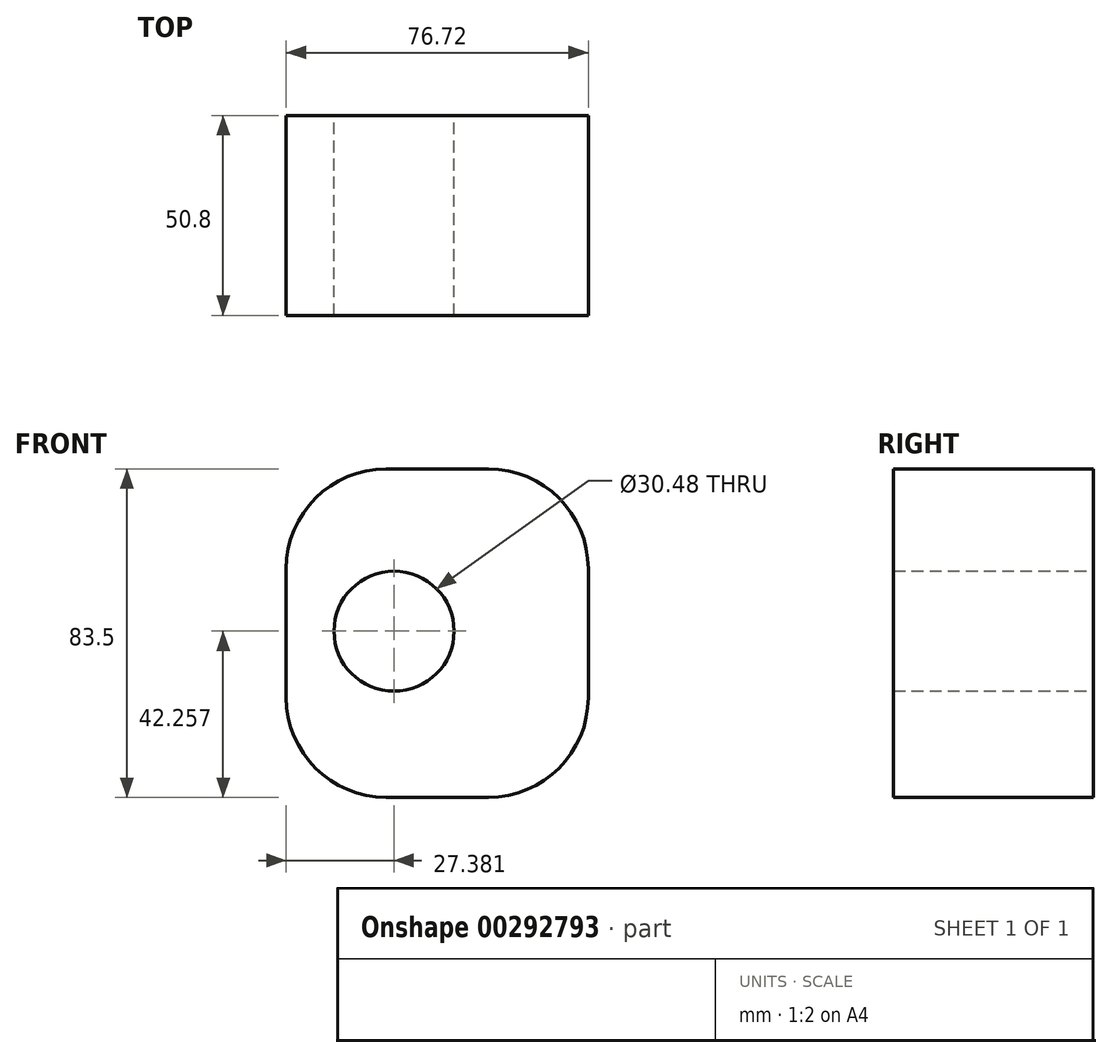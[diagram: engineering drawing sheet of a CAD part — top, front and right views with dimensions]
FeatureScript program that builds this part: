
annotation { "Feature Type Name" : "Feature", "Feature Type Description" : "" }
export const myFeature = defineFeature(function(context is Context, id is Id, definition is map)
    precondition{}
    {
        {
            var Q0;
            Q0=qCreatedBy(makeId("Front.planeOp"),FACE);
            var sketch = newSketch(context, id + "F0", { "sketchPlane" : qUnion([Q0])});
            skCircle(sketch, "E0", {"center": v(-49.34, 42.26) * mm, "radius": 15.24 * mm});
            skLineSegment(sketch, "E1.bottom", {"start": v(-51.32, 0) * mm, "end": v(-25.4, 0) * mm});
            skLineSegment(sketch, "E1.top", {"start": v(-51.32, 83.5) * mm, "end": v(-25.4, 83.5) * mm});
            skLineSegment(sketch, "E1.left", {"start": v(-76.72, 25.4) * mm, "end": v(-76.72, 58.1) * mm});
            skLineSegment(sketch, "E1.right", {"start": v(0, 25.4) * mm, "end": v(0, 58.1) * mm});
            skPoint(sketch, "E2.visualSharp", {"position": v(-76.72, 83.5) * mm});
            skArc(sketch, "E2.filletArc", {"start": v(-51.32, 83.5) * mm, "mid": v(-69.28, 76.06) * mm, "end": v(-76.72, 58.1) * mm});
            skPoint(sketch, "E3.visualSharp", {"position": v(0, 83.5) * mm});
            skArc(sketch, "E3.filletArc", {"start": v(0, 58.1) * mm, "mid": v(-7.44, 76.06) * mm, "end": v(-25.4, 83.5) * mm});
            skPoint(sketch, "E4.visualSharp", {"position": v(0, 0) * mm});
            skArc(sketch, "E4.filletArc", {"start": v(-25.4, 0) * mm, "mid": v(-7.44, 7.44) * mm, "end": v(0, 25.4) * mm});
            skPoint(sketch, "E5.visualSharp", {"position": v(-76.72, 0) * mm});
            skArc(sketch, "E5.filletArc", {"start": v(-76.72, 25.4) * mm, "mid": v(-69.28, 7.44) * mm, "end": v(-51.32, 0) * mm});
            skSolve(sketch);
        }
        {
            var Q0;
            Q0=makeQuery(id+"F0.imprint","IMPRINT",FACE,{"disambiguationData":[TD([[makeQuery(id+"F0.imprint","IMPRINT",EDGE,{"derivedFrom":sQuery(id+"F0.wireOp",EDGE,"E0")}),-1.0]])]});
            extrude(context, id + "F1", {"entities" : qUnion([Q0]), "endBound" : BoundingType.SYMMETRIC, "depth" : 50.8 * mm});
        }
    });
